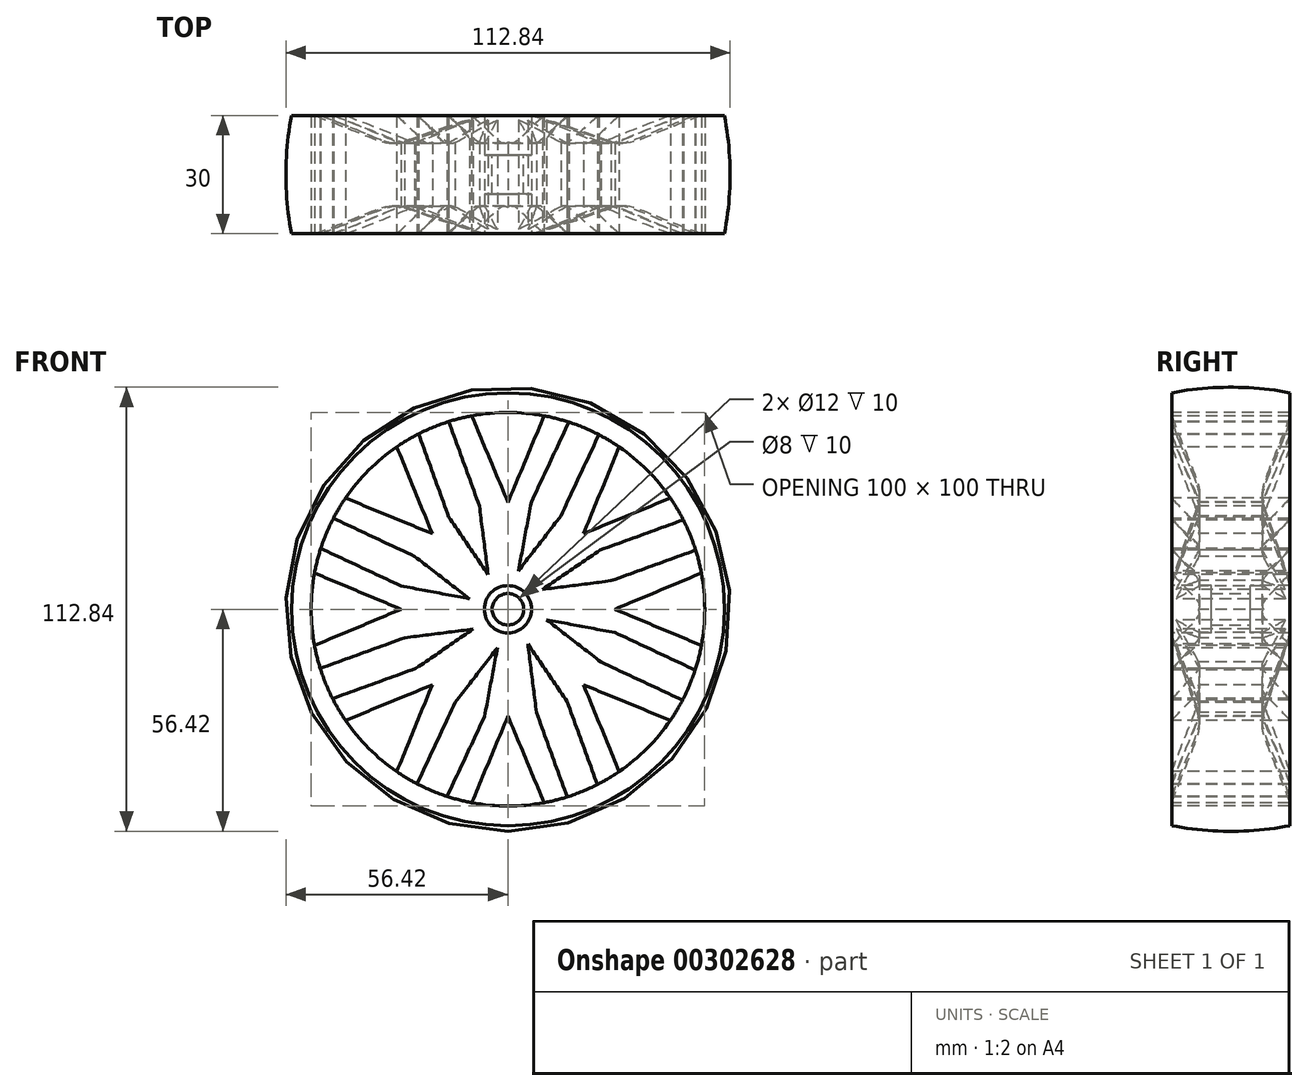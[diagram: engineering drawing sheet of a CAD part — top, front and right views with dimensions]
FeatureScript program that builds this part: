
annotation { "Feature Type Name" : "Feature", "Feature Type Description" : "" }
export const myFeature = defineFeature(function(context is Context, id is Id, definition is map)
    precondition{}
    {
        {
            var Q0;
            Q0=qCreatedBy(makeId("Right.planeOp"),FACE);
            var sketch = newSketch(context, id + "F0", { "sketchPlane" : qUnion([Q0])});
            skLineSegment(sketch, "E0", {"start": v(-36.11, 0) * mm, "end": v(38.72, 0) * mm});
            skSolve(sketch);
        }
        {
            var Q0;
            Q0=qCreatedBy(makeId("Right.planeOp"),FACE);
            var sketch = newSketch(context, id + "F1", { "sketchPlane" : qUnion([Q0])});
            skLineSegment(sketch, "E1.bottom", {"start": v(-15, 50) * mm, "end": v(15, 50) * mm});
            skLineSegment(sketch, "E1.top", {"start": v(-15, 55) * mm, "end": v(15, 55) * mm});
            skLineSegment(sketch, "E1.left", {"start": v(-15, 55) * mm, "end": v(-15, 50) * mm});
            skLineSegment(sketch, "E1.right", {"start": v(15, 55) * mm, "end": v(15, 50) * mm});
            skLineSegment(sketch, "E2", {"start": v(-15, 6) * mm, "end": v(15, 6) * mm});
            skLineSegment(sketch, "E3", {"start": v(-35, 58.63) * mm, "end": v(-35, -9.92) * mm});
            skCircle(sketch, "E4", {"center": v(0, -23.58) * mm, "radius": 80 * mm});
            skFitSpline(sketch, "E5", {"points": [v(15, 50) * mm, v(8, 30) * mm, v(9, 24.66) * mm, v(15, 6) * mm], "startDerivative": vector(-30.68, -90.02) * mm, "endDerivative": vector(15.2, -59.97) * mm});
            skLineSegment(sketch, "E6", {"start": v(0, 73.74) * mm, "end": v(0, -16.4) * mm});
            skLineSegment(sketch, "E7", {"start": v(-15, 83.9) * mm, "end": v(-15, 11.9) * mm});
            skFitSpline(sketch, "E8.MirrorCS", {"points": [v(-15, 50) * mm, v(-8, 30) * mm, v(-9, 24.66) * mm, v(-15, 6) * mm], "startDerivative": vector(30.68, -90.02) * mm, "endDerivative": vector(-15.2, -59.97) * mm});
            skLineSegment(sketch, "E9", {"start": v(15, 6) * mm, "end": v(15, 4) * mm});
            skLineSegment(sketch, "E10", {"start": v(-15, 6) * mm, "end": v(-15, 4) * mm});
            skLineSegment(sketch, "E11", {"start": v(15, 4) * mm, "end": v(-15, 4) * mm});
            skSolve(sketch);
        }
        {
            var Q0;
            {var subQ0=sQuery(id+"F1.wireOp",EDGE,"E4");var subQ3=sQuery(id+"F1.wireOp",EDGE,"E6");var subQ5=makeQuery(id+"F1.imprint","INTERSECT",VERTEX,{"derivedFrom":[subQ0,subQ3]});Q0=makeQuery(id+"F1.imprint","IMPRINT",FACE,{"disambiguationData":[TD([[makeQuery(id+"F1.imprint","IMPRINT",EDGE,{"disambiguationData":[TD([[subQ5,-1.0]])],"derivedFrom":subQ3}),-1.0]])]});}
            var Q1;
            {var subQ0=sQuery(id+"F1.wireOp",EDGE,"E4");var subQ3=sQuery(id+"F1.wireOp",EDGE,"E6");var subQ5=makeQuery(id+"F1.imprint","INTERSECT",VERTEX,{"derivedFrom":[subQ0,subQ3]});Q1=makeQuery(id+"F1.imprint","IMPRINT",FACE,{"disambiguationData":[TD([[makeQuery(id+"F1.imprint","IMPRINT",EDGE,{"disambiguationData":[TD([[subQ5,-1.0]])],"derivedFrom":subQ3}),1.0]])]});}
            var Q2;
            {var subQ1=sQuery(id+"F1.wireOp",EDGE,"E1.bottom");var subQ3=sQuery(id+"F1.wireOp",EDGE,"E6");var subQ4=makeQuery(id+"F1.imprint","INTERSECT",VERTEX,{"derivedFrom":[subQ1,subQ3]});Q2=makeQuery(id+"F1.imprint","IMPRINT",FACE,{"disambiguationData":[TD([[makeQuery(id+"F1.imprint","IMPRINT",EDGE,{"disambiguationData":[TD([[subQ4,1.0]])],"derivedFrom":subQ3}),-1.0]])]});}
            var Q3;
            {var subQ0=sQuery(id+"F1.wireOp",EDGE,"E1.right");Q3=makeQuery(id+"F1.imprint","IMPRINT",FACE,{"disambiguationData":[TD([[makeQuery(id+"F1.imprint","IMPRINT",EDGE,{"derivedFrom":subQ0}),-1.0]])]});}
            var Q4;
            {var subQ0=sQuery(id+"F1.wireOp",EDGE,"E8.MirrorCS");Q4=makeQuery(id+"F1.imprint","IMPRINT",FACE,{"disambiguationData":[TD([[makeQuery(id+"F1.imprint","IMPRINT",EDGE,{"derivedFrom":subQ0}),1.0]])]});}
            var Q5;
            {var subQ0=sQuery(id+"F1.wireOp",EDGE,"E5");Q5=makeQuery(id+"F1.imprint","IMPRINT",FACE,{"disambiguationData":[TD([[makeQuery(id+"F1.imprint","IMPRINT",EDGE,{"derivedFrom":subQ0}),-1.0]])]});}
            var Q6;
            Q6=sQuery(id+"F0.wireOp",EDGE,"E0");
            revolve(context, id + "F2", {"entities" : qUnion([Q0, Q1, Q2, Q3, Q4, Q5]), "axis" : qUnion([Q6]), "revolveType" : RevolveType.FULL});
        }
        {
            var Q0;
            Q0=qCreatedBy(makeId("Front.planeOp"),FACE);
            var sketch = newSketch(context, id + "F3", { "sketchPlane" : qUnion([Q0])});
            skLineSegment(sketch, "E12", {"start": v(0, 27.14) * mm, "end": v(-9.2, 49.15) * mm});
            skLineSegment(sketch, "E13.MirrorCS", {"start": v(0, 27.14) * mm, "end": v(9.2, 49.15) * mm});
            skLineSegment(sketch, "E14.1.0", {"start": v(-19.19, 19.19) * mm, "end": v(-28.25, 41.25) * mm});
            skLineSegment(sketch, "E14.1.1", {"start": v(-19.19, 19.19) * mm, "end": v(-41.25, 28.25) * mm});
            skLineSegment(sketch, "E14.2.0", {"start": v(-27.14, 0) * mm, "end": v(-49.15, 9.2) * mm});
            skLineSegment(sketch, "E14.2.1", {"start": v(-27.14, 0) * mm, "end": v(-49.15, -9.2) * mm});
            skLineSegment(sketch, "E14.3.0", {"start": v(-19.19, -19.19) * mm, "end": v(-41.25, -28.25) * mm});
            skLineSegment(sketch, "E14.3.1", {"start": v(-19.19, -19.19) * mm, "end": v(-28.25, -41.25) * mm});
            skLineSegment(sketch, "E14.4.0", {"start": v(0, -27.14) * mm, "end": v(-9.2, -49.15) * mm});
            skLineSegment(sketch, "E14.4.1", {"start": v(0, -27.14) * mm, "end": v(9.2, -49.15) * mm});
            skLineSegment(sketch, "E14.5.0", {"start": v(19.19, -19.19) * mm, "end": v(28.25, -41.25) * mm});
            skLineSegment(sketch, "E14.5.1", {"start": v(19.19, -19.19) * mm, "end": v(41.25, -28.25) * mm});
            skLineSegment(sketch, "E14.6.0", {"start": v(27.14, 0) * mm, "end": v(49.15, -9.2) * mm});
            skLineSegment(sketch, "E14.6.1", {"start": v(27.14, 0) * mm, "end": v(49.15, 9.2) * mm});
            skLineSegment(sketch, "E14.7.0", {"start": v(19.19, 19.19) * mm, "end": v(41.25, 28.25) * mm});
            skLineSegment(sketch, "E14.7.1", {"start": v(19.19, 19.19) * mm, "end": v(28.25, 41.25) * mm});
            skPoint(sketch, "E14.center", {"position": v(0, 0) * mm});
            skCircle(sketch, "E15", {"center": v(0, 0) * mm, "radius": 50 * mm});
            skLineSegment(sketch, "E16", {"start": v(-47.55, 15.45) * mm, "end": v(-27.19, 5.93) * mm});
            skLineSegment(sketch, "E17", {"start": v(-27.19, 5.93) * mm, "end": v(-23.68, 13.43) * mm});
            skLineSegment(sketch, "E18", {"start": v(-23.68, 13.43) * mm, "end": v(-44.35, 23.1) * mm});
            skLineSegment(sketch, "E19.1.0", {"start": v(-26.24, -7.25) * mm, "end": v(-47.69, -15.03) * mm});
            skLineSegment(sketch, "E19.1.1", {"start": v(-23.42, -15.03) * mm, "end": v(-26.24, -7.25) * mm});
            skLineSegment(sketch, "E19.1.2", {"start": v(-44.55, -22.7) * mm, "end": v(-23.42, -15.03) * mm});
            skLineSegment(sketch, "E19.2.0", {"start": v(-13.43, -23.68) * mm, "end": v(-23.1, -44.35) * mm});
            skLineSegment(sketch, "E19.2.1", {"start": v(-5.93, -27.19) * mm, "end": v(-13.43, -23.68) * mm});
            skLineSegment(sketch, "E19.2.2", {"start": v(-15.45, -47.55) * mm, "end": v(-5.93, -27.19) * mm});
            skLineSegment(sketch, "E19.3.0", {"start": v(7.25, -26.24) * mm, "end": v(15.03, -47.69) * mm});
            skLineSegment(sketch, "E19.3.1", {"start": v(15.03, -23.42) * mm, "end": v(7.25, -26.24) * mm});
            skLineSegment(sketch, "E19.3.2", {"start": v(22.7, -44.55) * mm, "end": v(15.03, -23.42) * mm});
            skLineSegment(sketch, "E19.4.0", {"start": v(23.68, -13.43) * mm, "end": v(44.35, -23.1) * mm});
            skLineSegment(sketch, "E19.4.1", {"start": v(27.19, -5.93) * mm, "end": v(23.68, -13.43) * mm});
            skLineSegment(sketch, "E19.4.2", {"start": v(47.55, -15.45) * mm, "end": v(27.19, -5.93) * mm});
            skLineSegment(sketch, "E19.5.0", {"start": v(26.24, 7.25) * mm, "end": v(47.69, 15.03) * mm});
            skLineSegment(sketch, "E19.5.1", {"start": v(23.42, 15.03) * mm, "end": v(26.24, 7.25) * mm});
            skLineSegment(sketch, "E19.5.2", {"start": v(44.55, 22.7) * mm, "end": v(23.42, 15.03) * mm});
            skLineSegment(sketch, "E19.6.0", {"start": v(13.43, 23.68) * mm, "end": v(23.1, 44.35) * mm});
            skLineSegment(sketch, "E19.6.1", {"start": v(5.93, 27.19) * mm, "end": v(13.43, 23.68) * mm});
            skLineSegment(sketch, "E19.6.2", {"start": v(15.45, 47.55) * mm, "end": v(5.93, 27.19) * mm});
            skLineSegment(sketch, "E19.7.0", {"start": v(-7.25, 26.24) * mm, "end": v(-15.03, 47.69) * mm});
            skLineSegment(sketch, "E19.7.1", {"start": v(-15.03, 23.42) * mm, "end": v(-7.25, 26.24) * mm});
            skLineSegment(sketch, "E19.7.2", {"start": v(-22.7, 44.55) * mm, "end": v(-15.03, 23.42) * mm});
            skLineSegment(sketch, "E20", {"start": v(-27.19, 5.93) * mm, "end": v(-9.79, 2.66) * mm});
            skLineSegment(sketch, "E21", {"start": v(-9.79, 2.66) * mm, "end": v(-23.68, 13.43) * mm});
            skLineSegment(sketch, "E22.1.0", {"start": v(-23.42, -15.03) * mm, "end": v(-8.8, -5.04) * mm});
            skLineSegment(sketch, "E22.1.1", {"start": v(-8.8, -5.04) * mm, "end": v(-26.24, -7.25) * mm});
            skLineSegment(sketch, "E22.2.0", {"start": v(-5.93, -27.19) * mm, "end": v(-2.66, -9.79) * mm});
            skLineSegment(sketch, "E22.2.1", {"start": v(-2.66, -9.79) * mm, "end": v(-13.43, -23.68) * mm});
            skLineSegment(sketch, "E22.3.0", {"start": v(15.03, -23.42) * mm, "end": v(5.04, -8.8) * mm});
            skLineSegment(sketch, "E22.3.1", {"start": v(5.04, -8.8) * mm, "end": v(7.25, -26.24) * mm});
            skLineSegment(sketch, "E22.4.0", {"start": v(27.19, -5.93) * mm, "end": v(9.79, -2.66) * mm});
            skLineSegment(sketch, "E22.4.1", {"start": v(9.79, -2.66) * mm, "end": v(23.68, -13.43) * mm});
            skLineSegment(sketch, "E22.5.0", {"start": v(23.42, 15.03) * mm, "end": v(8.8, 5.04) * mm});
            skLineSegment(sketch, "E22.5.1", {"start": v(8.8, 5.04) * mm, "end": v(26.24, 7.25) * mm});
            skLineSegment(sketch, "E22.6.0", {"start": v(5.93, 27.19) * mm, "end": v(2.66, 9.79) * mm});
            skLineSegment(sketch, "E22.6.1", {"start": v(2.66, 9.79) * mm, "end": v(13.43, 23.68) * mm});
            skLineSegment(sketch, "E22.7.0", {"start": v(-15.03, 23.42) * mm, "end": v(-5.04, 8.8) * mm});
            skLineSegment(sketch, "E22.7.1", {"start": v(-5.04, 8.8) * mm, "end": v(-7.25, 26.24) * mm});
            skSolve(sketch);
        }
        {
            var Q0;
            {var subQ0=sQuery(id+"F3.wireOp",EDGE,"E12");Q0=makeQuery(id+"F3.imprint","IMPRINT",FACE,{"disambiguationData":[TD([[makeQuery(id+"F3.imprint","IMPRINT",EDGE,{"derivedFrom":subQ0}),-1.0]])]});}
            var Q1;
            {var subQ0=sQuery(id+"F3.wireOp",EDGE,"E14.1.0");Q1=makeQuery(id+"F3.imprint","IMPRINT",FACE,{"disambiguationData":[TD([[makeQuery(id+"F3.imprint","IMPRINT",EDGE,{"derivedFrom":subQ0}),1.0]])]});}
            var Q2;
            {var subQ0=sQuery(id+"F3.wireOp",EDGE,"E14.2.0");Q2=makeQuery(id+"F3.imprint","IMPRINT",FACE,{"disambiguationData":[TD([[makeQuery(id+"F3.imprint","IMPRINT",EDGE,{"derivedFrom":subQ0}),1.0]])]});}
            var Q3;
            {var subQ0=sQuery(id+"F3.wireOp",EDGE,"E14.3.0");Q3=makeQuery(id+"F3.imprint","IMPRINT",FACE,{"disambiguationData":[TD([[makeQuery(id+"F3.imprint","IMPRINT",EDGE,{"derivedFrom":subQ0}),1.0]])]});}
            var Q4;
            {var subQ0=sQuery(id+"F3.wireOp",EDGE,"E14.4.0");Q4=makeQuery(id+"F3.imprint","IMPRINT",FACE,{"disambiguationData":[TD([[makeQuery(id+"F3.imprint","IMPRINT",EDGE,{"derivedFrom":subQ0}),1.0]])]});}
            var Q5;
            {var subQ0=sQuery(id+"F3.wireOp",EDGE,"E14.5.0");Q5=makeQuery(id+"F3.imprint","IMPRINT",FACE,{"disambiguationData":[TD([[makeQuery(id+"F3.imprint","IMPRINT",EDGE,{"derivedFrom":subQ0}),1.0]])]});}
            var Q6;
            {var subQ0=sQuery(id+"F3.wireOp",EDGE,"E14.6.0");Q6=makeQuery(id+"F3.imprint","IMPRINT",FACE,{"disambiguationData":[TD([[makeQuery(id+"F3.imprint","IMPRINT",EDGE,{"derivedFrom":subQ0}),1.0]])]});}
            var Q7;
            {var subQ0=sQuery(id+"F3.wireOp",EDGE,"E14.7.0");Q7=makeQuery(id+"F3.imprint","IMPRINT",FACE,{"disambiguationData":[TD([[makeQuery(id+"F3.imprint","IMPRINT",EDGE,{"derivedFrom":subQ0}),1.0]])]});}
            var Q8;
            Q8=makeQuery(id+"F3.imprint","IMPRINT",FACE,{"disambiguationData":[TD([[makeQuery(id+"F3.imprint","IMPRINT",EDGE,{"derivedFrom":sQuery(id+"F3.wireOp",EDGE,"E19.5.1")}),-1.0]])]});
            var Q9;
            {var subQ0=sQuery(id+"F3.wireOp",EDGE,"E19.5.0");Q9=makeQuery(id+"F3.imprint","IMPRINT",FACE,{"disambiguationData":[TD([[makeQuery(id+"F3.imprint","IMPRINT",EDGE,{"derivedFrom":subQ0}),1.0]])]});}
            var Q10;
            {var subQ0=sQuery(id+"F3.wireOp",EDGE,"E19.6.0");Q10=makeQuery(id+"F3.imprint","IMPRINT",FACE,{"disambiguationData":[TD([[makeQuery(id+"F3.imprint","IMPRINT",EDGE,{"derivedFrom":subQ0}),1.0]])]});}
            var Q11;
            Q11=makeQuery(id+"F3.imprint","IMPRINT",FACE,{"disambiguationData":[TD([[makeQuery(id+"F3.imprint","IMPRINT",EDGE,{"derivedFrom":sQuery(id+"F3.wireOp",EDGE,"E19.6.1")}),-1.0]])]});
            var Q12;
            {var subQ0=sQuery(id+"F3.wireOp",EDGE,"E19.7.0");Q12=makeQuery(id+"F3.imprint","IMPRINT",FACE,{"disambiguationData":[TD([[makeQuery(id+"F3.imprint","IMPRINT",EDGE,{"derivedFrom":subQ0}),1.0]])]});}
            var Q13;
            Q13=makeQuery(id+"F3.imprint","IMPRINT",FACE,{"disambiguationData":[TD([[makeQuery(id+"F3.imprint","IMPRINT",EDGE,{"derivedFrom":sQuery(id+"F3.wireOp",EDGE,"E19.7.1")}),-1.0]])]});
            var Q14;
            Q14=makeQuery(id+"F3.imprint","IMPRINT",FACE,{"disambiguationData":[TD([[makeQuery(id+"F3.imprint","IMPRINT",EDGE,{"derivedFrom":sQuery(id+"F3.wireOp",EDGE,"E17")}),-1.0]])]});
            var Q15;
            {var subQ0=sQuery(id+"F3.wireOp",EDGE,"E16");Q15=makeQuery(id+"F3.imprint","IMPRINT",FACE,{"disambiguationData":[TD([[makeQuery(id+"F3.imprint","IMPRINT",EDGE,{"derivedFrom":subQ0}),1.0]])]});}
            var Q16;
            Q16=makeQuery(id+"F3.imprint","IMPRINT",FACE,{"disambiguationData":[TD([[makeQuery(id+"F3.imprint","IMPRINT",EDGE,{"derivedFrom":sQuery(id+"F3.wireOp",EDGE,"E19.1.1")}),-1.0]])]});
            var Q17;
            {var subQ0=sQuery(id+"F3.wireOp",EDGE,"E19.1.0");Q17=makeQuery(id+"F3.imprint","IMPRINT",FACE,{"disambiguationData":[TD([[makeQuery(id+"F3.imprint","IMPRINT",EDGE,{"derivedFrom":subQ0}),1.0]])]});}
            var Q18;
            {var subQ0=sQuery(id+"F3.wireOp",EDGE,"E19.2.0");Q18=makeQuery(id+"F3.imprint","IMPRINT",FACE,{"disambiguationData":[TD([[makeQuery(id+"F3.imprint","IMPRINT",EDGE,{"derivedFrom":subQ0}),1.0]])]});}
            var Q19;
            Q19=makeQuery(id+"F3.imprint","IMPRINT",FACE,{"disambiguationData":[TD([[makeQuery(id+"F3.imprint","IMPRINT",EDGE,{"derivedFrom":sQuery(id+"F3.wireOp",EDGE,"E19.2.1")}),-1.0]])]});
            var Q20;
            Q20=makeQuery(id+"F3.imprint","IMPRINT",FACE,{"disambiguationData":[TD([[makeQuery(id+"F3.imprint","IMPRINT",EDGE,{"derivedFrom":sQuery(id+"F3.wireOp",EDGE,"E19.3.1")}),-1.0]])]});
            var Q21;
            {var subQ0=sQuery(id+"F3.wireOp",EDGE,"E19.3.0");Q21=makeQuery(id+"F3.imprint","IMPRINT",FACE,{"disambiguationData":[TD([[makeQuery(id+"F3.imprint","IMPRINT",EDGE,{"derivedFrom":subQ0}),1.0]])]});}
            var Q22;
            {var subQ0=sQuery(id+"F3.wireOp",EDGE,"E19.4.0");Q22=makeQuery(id+"F3.imprint","IMPRINT",FACE,{"disambiguationData":[TD([[makeQuery(id+"F3.imprint","IMPRINT",EDGE,{"derivedFrom":subQ0}),1.0]])]});}
            var Q23;
            Q23=makeQuery(id+"F3.imprint","IMPRINT",FACE,{"disambiguationData":[TD([[makeQuery(id+"F3.imprint","IMPRINT",EDGE,{"derivedFrom":sQuery(id+"F3.wireOp",EDGE,"E19.4.1")}),-1.0]])]});
            extrude(context, id + "F4", {"entities" : qUnion([Q0, Q1, Q2, Q3, Q4, Q5, Q6, Q7, Q8, Q9, Q10, Q11, Q12, Q13, Q14, Q15, Q16, Q17, Q18, Q19, Q20, Q21, Q22, Q23]), "operationType" : NewBodyOperationType.REMOVE, "endBound" : BoundingType.SYMMETRIC, "oppositeDirection" : true, "depth" : 100 * mm});
        }
        {
            var Q0;
            Q0=qCreatedBy(makeId("Front.planeOp"),FACE);
            var sketch = newSketch(context, id + "F5", { "sketchPlane" : qUnion([Q0])});
            skCircle(sketch, "E23", {"center": v(0, 0) * mm, "radius": 6 * mm});
            skCircle(sketch, "E24", {"center": v(0, 0) * mm, "radius": 4 * mm});
            skSolve(sketch);
        }
        {
            var Q0;
            Q0 = qSketchRegion(id + "F5", true);
            extrude(context, id + "F6", {"entities" : qUnion([Q0]), "operationType" : NewBodyOperationType.ADD, "endBound" : BoundingType.SYMMETRIC, "depth" : 10 * mm});
        }
    });
